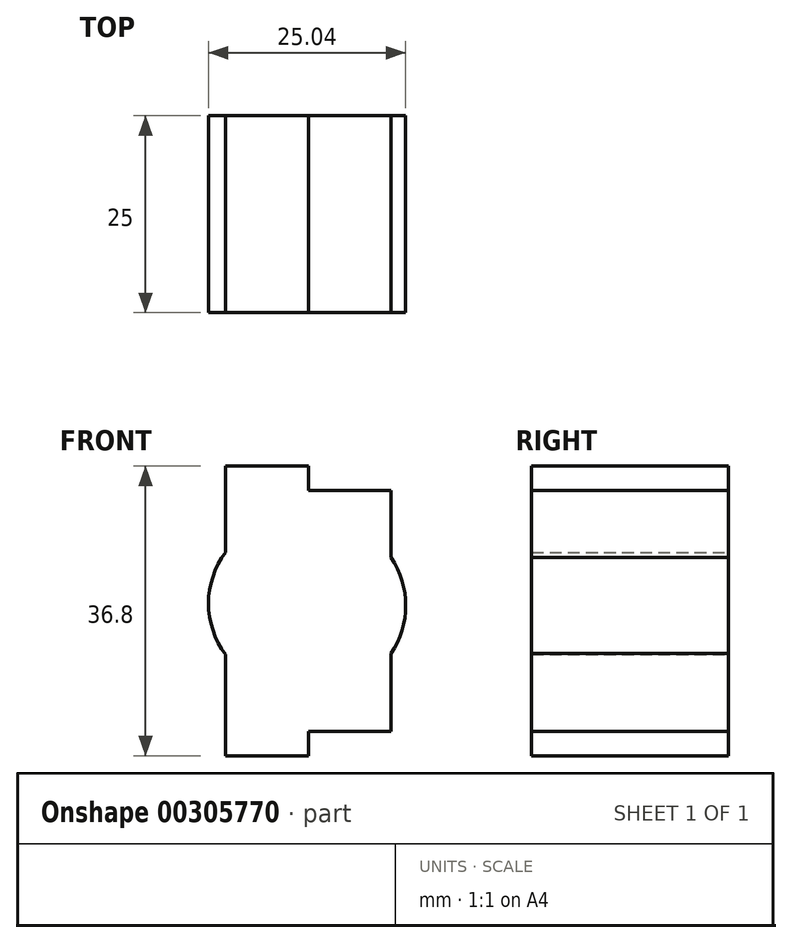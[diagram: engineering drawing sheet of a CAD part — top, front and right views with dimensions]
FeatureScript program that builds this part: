
annotation { "Feature Type Name" : "Feature", "Feature Type Description" : "" }
export const myFeature = defineFeature(function(context is Context, id is Id, definition is map)
    precondition{}
    {
        {
            var Q0;
            Q0=qCreatedBy(makeId("Front.planeOp"),FACE);
            var sketch = newSketch(context, id + "F0", { "sketchPlane" : qUnion([Q0])});
            skLineSegment(sketch, "E0", {"start": v(-10.5, -18.4) * mm, "end": v(0, -18.4) * mm});
            skLineSegment(sketch, "E1", {"start": v(0, -18.4) * mm, "end": v(0, -15.3) * mm});
            skLineSegment(sketch, "E2", {"start": v(0, -15.3) * mm, "end": v(10.5, -15.3) * mm});
            skLineSegment(sketch, "E3", {"start": v(10.5, -15.3) * mm, "end": v(10.5, -5.42) * mm});
            skLineSegment(sketch, "E4", {"start": v(-10.5, -18.4) * mm, "end": v(-10.5, -5.55) * mm});
            skArc(sketch, "E5", {"start": v(-10.5, 7.45) * mm, "mid": v(-12.68, 0.95) * mm, "end": v(-10.5, -5.55) * mm});
            skLineSegment(sketch, "E6", {"start": v(-10.5, 7.45) * mm, "end": v(-10.5, 18.4) * mm});
            skLineSegment(sketch, "E7", {"start": v(-10.5, 18.4) * mm, "end": v(0, 18.4) * mm});
            skLineSegment(sketch, "E8", {"start": v(0, 18.4) * mm, "end": v(0, 15.3) * mm});
            skArc(sketch, "E9", {"start": v(10.5, -5.42) * mm, "mid": v(12.36, 0.68) * mm, "end": v(10.5, 6.77) * mm});
            skLineSegment(sketch, "E10", {"start": v(10.5, 6.77) * mm, "end": v(10.5, 15.3) * mm});
            skLineSegment(sketch, "E11", {"start": v(0, 15.3) * mm, "end": v(10.5, 15.3) * mm});
            skSolve(sketch);
        }
        {
            var Q0;
            Q0 = qSketchRegion(id + "F0", true);
            extrude(context, id + "F1", {"entities" : qUnion([Q0]), "depth" : 25 * mm});
        }
    });
